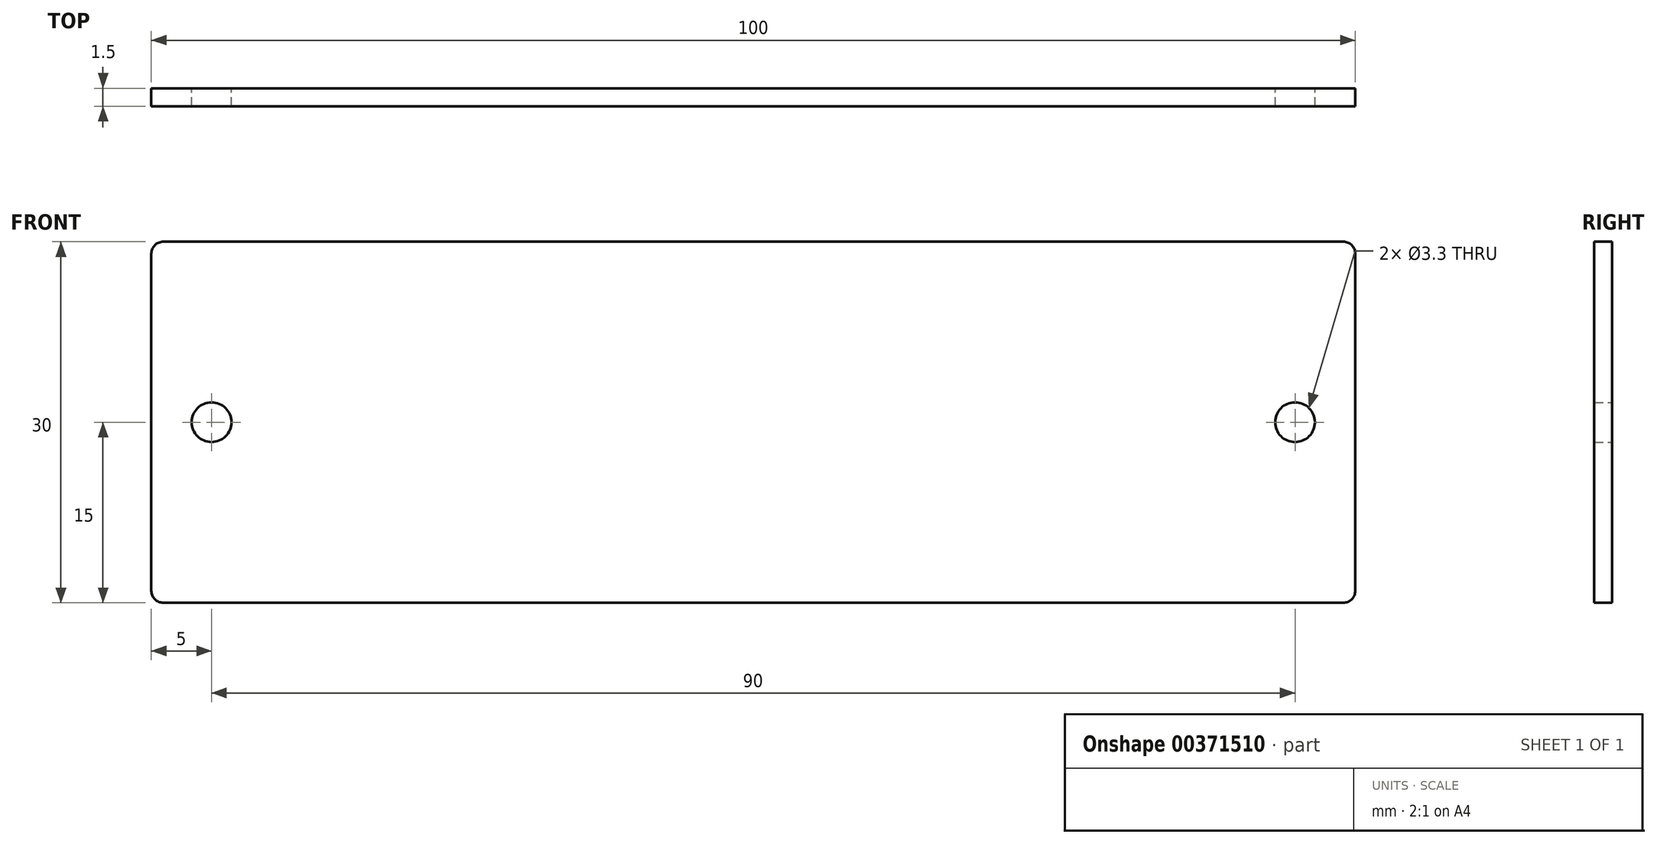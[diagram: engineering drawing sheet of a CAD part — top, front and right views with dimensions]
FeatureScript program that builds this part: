
annotation { "Feature Type Name" : "Feature", "Feature Type Description" : "" }
export const myFeature = defineFeature(function(context is Context, id is Id, definition is map)
    precondition{}
    {
        {
            var Q0;
            Q0=qCreatedBy(makeId("Front.planeOp"),FACE);
            var sketch = newSketch(context, id + "F0", { "sketchPlane" : qUnion([Q0])});
            skLineSegment(sketch, "E0.bottom", {"start": v(-50, 15) * mm, "end": v(0, 15) * mm});
            skLineSegment(sketch, "E0.top", {"start": v(-50, -15) * mm, "end": v(0, -15) * mm});
            skLineSegment(sketch, "E0.left", {"start": v(-50, 15) * mm, "end": v(-50, -15) * mm});
            skPoint(sketch, "E0.middle", {"position": v(0, 0) * mm});
            skLineSegment(sketch, "E1", {"start": v(-54.34, 0) * mm, "end": v(56.42, 0) * mm, "construction": true});
            skCircle(sketch, "E2", {"center": v(-45, 0) * mm, "radius": 1.65 * mm});
            skLineSegment(sketch, "E3", {"start": v(0, 25.3) * mm, "end": v(0, -35.13) * mm, "construction": true});
            skLineSegment(sketch, "E4.MirrorCS", {"start": v(50, 15) * mm, "end": v(50, -15) * mm});
            skLineSegment(sketch, "E5.MirrorCS", {"start": v(50, 15) * mm, "end": v(0, 15) * mm});
            skLineSegment(sketch, "E6.MirrorCS", {"start": v(50, -15) * mm, "end": v(0, -15) * mm});
            skCircle(sketch, "E7.MirrorC", {"center": v(45, 0) * mm, "radius": 1.65 * mm});
            skSolve(sketch);
        }
        {
            var Q0;
            Q0=makeQuery(id+"F0.imprint","IMPRINT",FACE,{"disambiguationData":[TD([[makeQuery(id+"F0.imprint","IMPRINT",EDGE,{"derivedFrom":sQuery(id+"F0.wireOp",EDGE,"E0.bottom")}),-1.0]])]});
            extrude(context, id + "F1", {"entities" : qUnion([Q0]), "depth" : 1.5 * mm, "offsetDistance" : 25 * mm});
        }
        {
            var Q0;
            Q0=makeQuery(id+"F1.opExtrude","SWEPT_EDGE",EDGE,{"disambiguationData":[OSD([sQuery(id+"F0.wireOp",EDGE,"E4.MirrorCS"),sQuery(id+"F0.wireOp",EDGE,"E5.MirrorCS")])]});
            var Q1;
            Q1=makeQuery(id+"F1.opExtrude","SWEPT_EDGE",EDGE,{"disambiguationData":[OSD([sQuery(id+"F0.wireOp",EDGE,"E4.MirrorCS"),sQuery(id+"F0.wireOp",EDGE,"E6.MirrorCS")])]});
            var Q2;
            Q2=makeQuery(id+"F1.opExtrude","SWEPT_EDGE",EDGE,{"disambiguationData":[OSD([sQuery(id+"F0.wireOp",EDGE,"E0.bottom"),sQuery(id+"F0.wireOp",EDGE,"E0.left")])]});
            var Q3;
            Q3=makeQuery(id+"F1.opExtrude","SWEPT_EDGE",EDGE,{"disambiguationData":[OSD([sQuery(id+"F0.wireOp",EDGE,"E0.top"),sQuery(id+"F0.wireOp",EDGE,"E0.left")])]});
            fillet(context, id + "F2", {"entities" : qUnion([Q0, Q1, Q2, Q3]), "tangentPropagation" : true, "radius" : 1 * mm, "defaultsChanged" : false, "vertexSettings" : [], "allowEdgeOverflow" : false});
        }
    });
